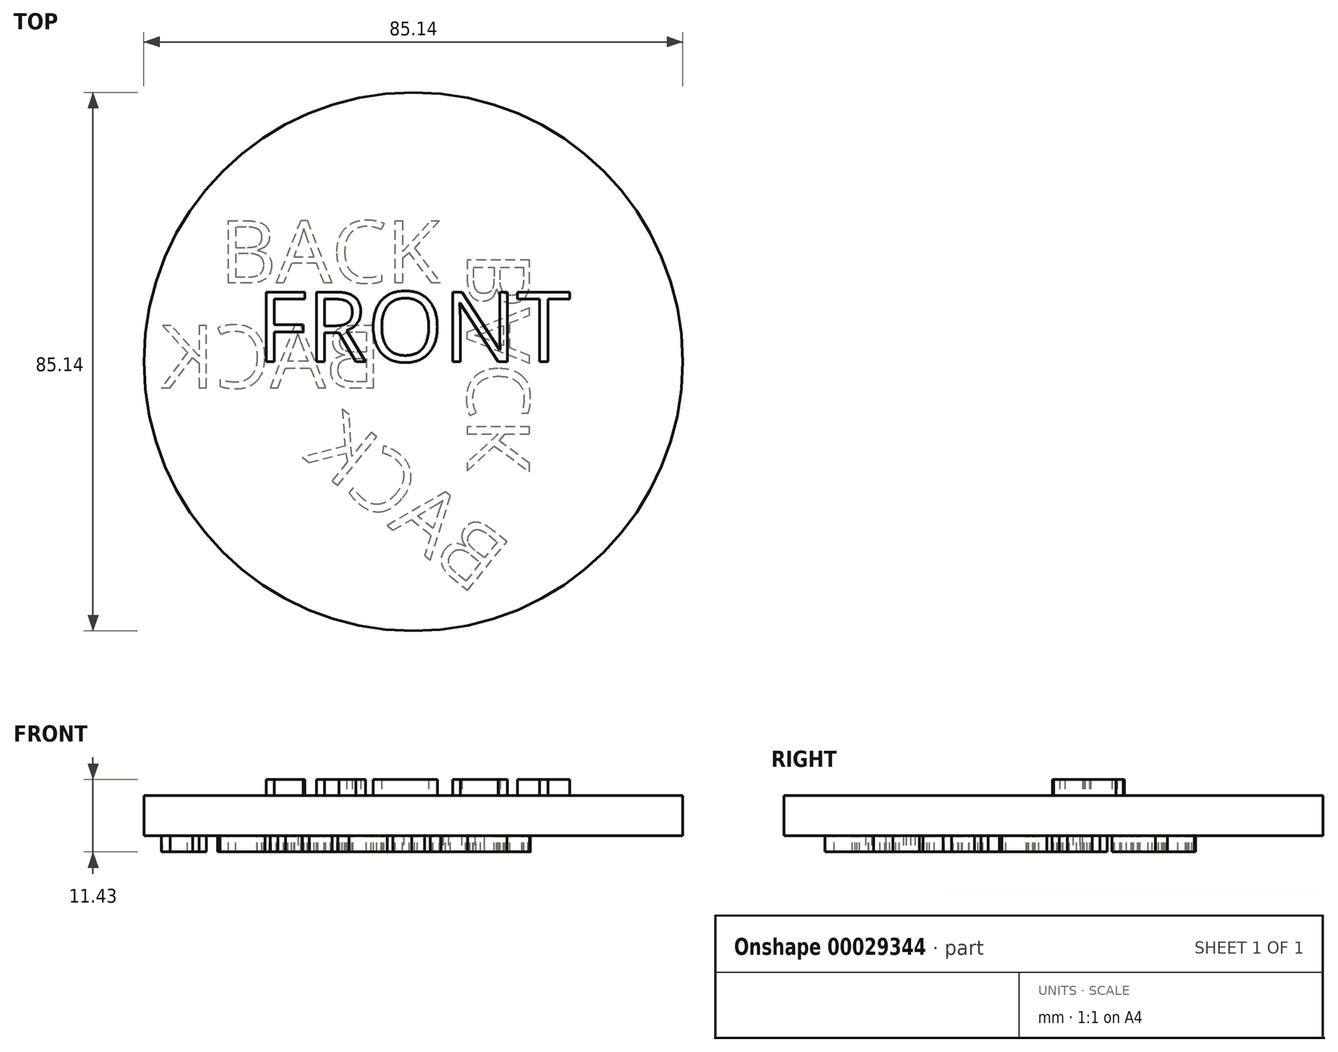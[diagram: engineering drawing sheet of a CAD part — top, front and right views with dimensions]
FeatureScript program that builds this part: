
annotation { "Feature Type Name" : "Feature", "Feature Type Description" : "" }
export const myFeature = defineFeature(function(context is Context, id is Id, definition is map)
    precondition{}
    {
        {
            var Q0;
            Q0=qCreatedBy(makeId("Top.planeOp"),FACE);
            var sketch = newSketch(context, id + "F0", { "sketchPlane" : qUnion([Q0])});
            skCircle(sketch, "E0", {"center": v(0, 0) * mm, "radius": 42.57 * mm});
            skSolve(sketch);
        }
        {
            var Q0;
            Q0=makeQuery(id+"F0.imprint","IMPRINT",FACE,{"disambiguationData":[TD([[makeQuery(id+"F0.imprint","IMPRINT",EDGE,{"derivedFrom":sQuery(id+"F0.wireOp",EDGE,"E0")}),1.0]])]});
            extrude(context, id + "F1", {"entities" : qUnion([Q0]), "depth" : 6.35 * mm});
        }
        {
            var Q0;
            Q0=makeQuery(id+"F1.opExtrude","CAP_FACE",FACE,{"disambiguationData":[OSD([sQuery(id+"F0.wireOp",EDGE,"E0")])],"isStart":false});
            var sketch = newSketch(context, id + "F2", { "sketchPlane" : qUnion([Q0])});
            skText(sketch, "E1", { "text": "FRONT", "fontName": "OpenSans-Regular.ttf"});
            const initialGuessF2  = {"E1": [-0.02476, 0, 1, 0, 0.0111]};
            skSetInitialGuess(sketch, initialGuessF2);
            skSolve(sketch);
        }
        {
            var Q0;
            Q0=qSketchRegion(id+"F2",true);
            extrude(context, id + "F3", {"entities" : qUnion([Q0]), "operationType" : NewBodyOperationType.ADD, "depth" : 2.54 * mm});
        }
        {
            var Q0;
            Q0=makeQuery(id+"F1.opExtrude","CAP_FACE",FACE,{"disambiguationData":[OSD([sQuery(id+"F0.wireOp",EDGE,"E0")])],"isStart":true});
            var sketch = newSketch(context, id + "F4", { "sketchPlane" : qUnion([Q0])});
            skText(sketch, "E2", { "text": "BACK", "fontName": "OpenSans-Regular.ttf"});
            skText(sketch, "E3", { "text": "BACK", "fontName": "OpenSans-Regular.ttf"});
            skText(sketch, "E4", { "text": "BACK", "fontName": "OpenSans-Regular.ttf"});
            const initialGuessF4  = {"E2": [-0.00492, 0.00414, -1, 0, 0.00994], "E3": [0.01838, -0.01744, 0, 1, 0.00994], "E4": [0.00965, 0.03698, -0.77875, -0.62733, 0.00994]};
            skSetInitialGuess(sketch, initialGuessF4);
            skSolve(sketch);
        }
        {
            var Q0;
            Q0=qSketchRegion(id+"F4",true);
            extrude(context, id + "F5", {"entities" : qUnion([Q0]), "operationType" : NewBodyOperationType.ADD, "depth" : 2.54 * mm});
        }
        {
            var Q0;
            {var subQ0=sQuery(id+"F0.wireOp",EDGE,"E0");Q0=makeQuery(id+"F3.boolean.opBoolean","SPLIT",FACE,{"disambiguationData":[TD([makeQuery(id+"F1.opExtrude","SWEPT_FACE",FACE,{"disambiguationData":[OSD([subQ0])]})])],"derivedFrom":makeQuery(id+"F1.opExtrude","CAP_FACE",FACE,{"disambiguationData":[OSD([subQ0])],"isStart":false})});}
            var sketch = newSketch(context, id + "F6", { "sketchPlane" : qUnion([Q0])});
            skText(sketch, "E5", { "text": "BACK\n", "fontName": "OpenSans-Regular.ttf"});
            const initialGuessF6  = {"E5": [-0.03058, 0.01242, 1, 0, 0.00994]};
            skSetInitialGuess(sketch, initialGuessF6);
            skSolve(sketch);
        }
        {
            var Q0;
            Q0=qSketchRegion(id+"F6",true);
            var Q1;
            Q1=makeQuery(id+"F5.opExtrude","CAP_FACE",FACE,{"disambiguationData":[OSD([sQuery(id+"F4.wireOp",EDGE,"E2.sketch_text.stroke-0"),sQuery(id+"F4.wireOp",EDGE,"E2.sketch_text.stroke-1"),sQuery(id+"F4.wireOp",EDGE,"E2.sketch_text.stroke-2"),sQuery(id+"F4.wireOp",EDGE,"E2.sketch_text.stroke-3"),sQuery(id+"F4.wireOp",EDGE,"E2.sketch_text.stroke-4"),sQuery(id+"F4.wireOp",EDGE,"E2.sketch_text.stroke-5"),sQuery(id+"F4.wireOp",EDGE,"E2.sketch_text.stroke-6"),sQuery(id+"F4.wireOp",EDGE,"E2.sketch_text.stroke-7"),sQuery(id+"F4.wireOp",EDGE,"E2.sketch_text.stroke-8"),sQuery(id+"F4.wireOp",EDGE,"E2.sketch_text.stroke-9"),sQuery(id+"F4.wireOp",EDGE,"E2.sketch_text.stroke-10"),sQuery(id+"F4.wireOp",EDGE,"E2.sketch_text.stroke-11"),sQuery(id+"F4.wireOp",EDGE,"E2.sketch_text.stroke-12"),sQuery(id+"F4.wireOp",EDGE,"E2.sketch_text.stroke-13"),sQuery(id+"F4.wireOp",EDGE,"E2.sketch_text.stroke-14"),sQuery(id+"F4.wireOp",EDGE,"E2.sketch_text.stroke-15"),sQuery(id+"F4.wireOp",EDGE,"E2.sketch_text.stroke-16"),sQuery(id+"F4.wireOp",EDGE,"E2.sketch_text.stroke-17"),sQuery(id+"F4.wireOp",EDGE,"E2.sketch_text.stroke-18"),sQuery(id+"F4.wireOp",EDGE,"E2.sketch_text.stroke-19"),sQuery(id+"F4.wireOp",EDGE,"E2.sketch_text.stroke-20"),sQuery(id+"F4.wireOp",EDGE,"E2.sketch_text.stroke-21"),sQuery(id+"F4.wireOp",EDGE,"E2.sketch_text.stroke-22"),sQuery(id+"F4.wireOp",EDGE,"E2.sketch_text.stroke-23"),sQuery(id+"F4.wireOp",EDGE,"E2.sketch_text.stroke-24")])],"isStart":false});
            extrude(context, id + "F7", {"entities" : qUnion([Q0]), "operationType" : NewBodyOperationType.ADD, "endBound" : BoundingType.UP_TO_SURFACE, "oppositeDirection" : true, "endBoundEntityFace" : qUnion([Q1]), "depth" : 25.4 * mm});
        }
    });
